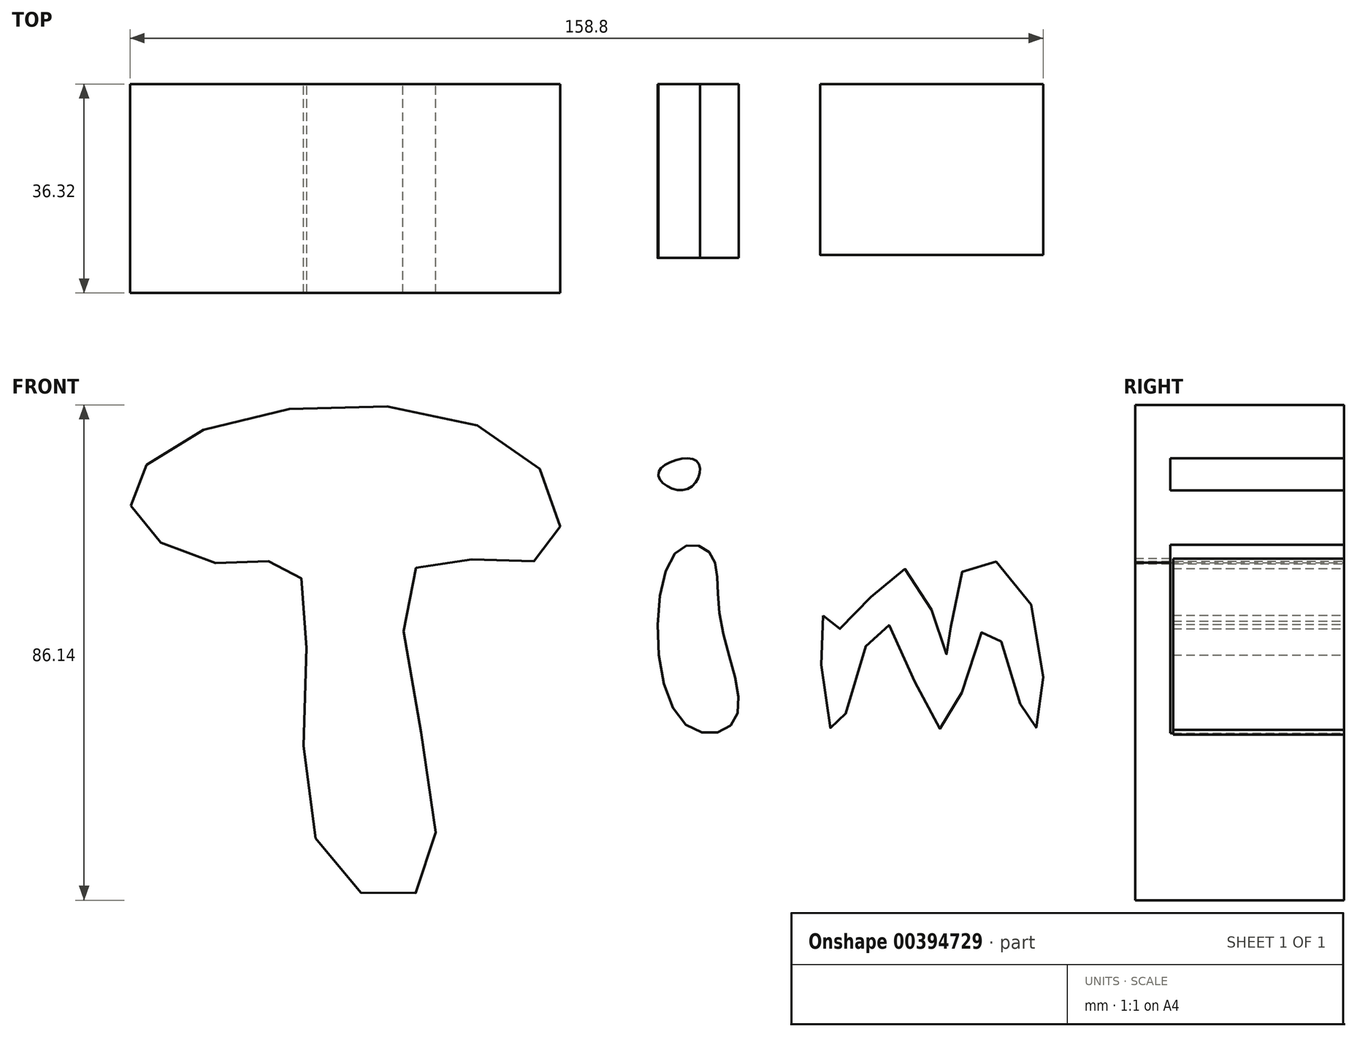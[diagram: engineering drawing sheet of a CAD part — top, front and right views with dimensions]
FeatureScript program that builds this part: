
annotation { "Feature Type Name" : "Feature", "Feature Type Description" : "" }
export const myFeature = defineFeature(function(context is Context, id is Id, definition is map)
    precondition{}
    {
        {
            var Q0;
            Q0=qCreatedBy(makeId("Front.planeOp"),FACE);
            var sketch = newSketch(context, id + "F0", { "sketchPlane" : qUnion([Q0])});
            skFitSpline(sketch, "E0", {"points": [v(-58.4, 45.31) * mm, v(-42.85, 35.27) * mm, v(-29.2, 33.56) * mm, v(-24.65, -16.12) * mm, v(-6.64, -19.53) * mm, v(-9.48, 33.75) * mm, v(13.27, 36.21) * mm, v(10.8, 53.85) * mm, v(-42.85, 59.53) * mm, v(-58.4, 45.31) * mm]});
            skSolve(sketch);
        }
        {
            var Q0;
            Q0 = qSketchRegion(id + "F0", true);
            extrude(context, id + "F1", {"entities" : qUnion([Q0]), "depth" : 36.32 * mm});
        }
        {
            var Q0;
            Q0=qCreatedBy(makeId("Front.planeOp"),FACE);
            var sketch = newSketch(context, id + "F2", { "sketchPlane" : qUnion([Q0])});
            skFitSpline(sketch, "E1", {"points": [v(36.21, 36.97) * mm, v(37.35, 7.96) * mm, v(46.64, 7.96) * mm, v(44.18, 25.4) * mm, v(42.28, 37.16) * mm, v(36.21, 36.97) * mm]});
            skFitSpline(sketch, "E2", {"points": [v(40, 53.09) * mm, v(33.37, 51) * mm, v(38.3, 48.16) * mm, v(40, 53.09) * mm]});
            skSolve(sketch);
        }
        {
            var Q0;
            Q0 = qSketchRegion(id + "F2", true);
            extrude(context, id + "F3", {"entities" : qUnion([Q0]), "depth" : 30.23 * mm});
        }
        {
            var Q0;
            Q0=qCreatedBy(makeId("Front.planeOp"),FACE);
            var sketch = newSketch(context, id + "F4", { "sketchPlane" : qUnion([Q0])});
            skFitSpline(sketch, "E3", {"points": [v(62, 26.16) * mm, v(64.08, 5.5) * mm, v(72.24, 25.22) * mm, v(82.66, 6.45) * mm, v(90.82, 24.65) * mm, v(98.21, 6.45) * mm, v(97.83, 29) * mm, v(86.65, 34.5) * mm, v(83.61, 19.34) * mm, v(76.22, 34.32) * mm, v(64.84, 23.89) * mm, v(62, 26.16) * mm]});
            skSolve(sketch);
        }
        {
            var Q0;
            Q0 = qSketchRegion(id + "F4", true);
            extrude(context, id + "F5", {"entities" : qUnion([Q0]), "depth" : 29.72 * mm});
        }
    });
